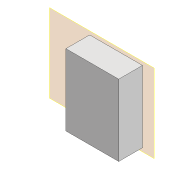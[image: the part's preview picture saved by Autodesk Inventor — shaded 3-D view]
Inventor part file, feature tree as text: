
AUTODESK INVENTOR PART (.ipt)
format: ipt  version: 2020 (Build 240168000, 168)  size: 77,312 bytes
history: native  units: mm
features: other x5, extrude x1, sketch x1
ambient origin geometry x8: Origin, YZ Plane, XZ Plane, XY Plane, X Axis, Y Axis, Z Axis, Center Point
bodies: Body1 (feature_tree)
feature tree (7):
  other  "Sólido1"
  other  "Plano de trabalho1"
  extrude  "Extrusão1"  [1 undecoded]
  sketch  "Esboço1"  dims[d0=50.0mm d1=0.0mm]
  other  "Referência1"
  other  "Montagem1"
  other  "Base:2"
note: 1 required parameter value undecoded (feature->parameter linkage not recoverable at this tier; creation-order binding heuristic only, values carry confidence <= 0.55)
